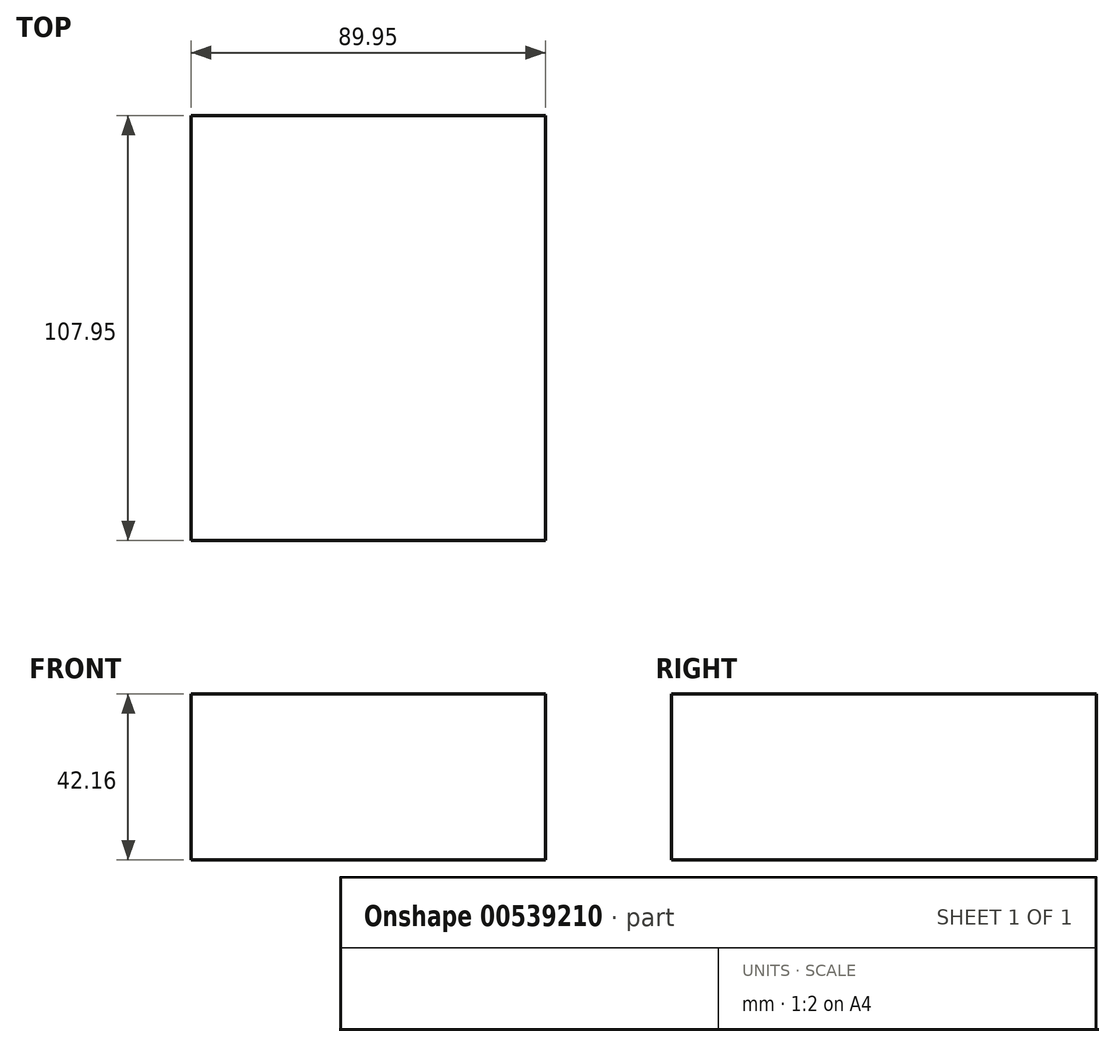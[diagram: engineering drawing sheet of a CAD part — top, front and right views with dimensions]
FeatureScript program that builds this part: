
annotation { "Feature Type Name" : "Feature", "Feature Type Description" : "" }
export const myFeature = defineFeature(function(context is Context, id is Id, definition is map)
    precondition{}
    {
        {
            var Q0;
            Q0=qCreatedBy(makeId("Top.planeOp"),FACE);
            var sketch = newSketch(context, id + "F0", { "sketchPlane" : qUnion([Q0])});
            skLineSegment(sketch, "E0.bottom", {"start": v(-52.77, 49.57) * mm, "end": v(37.18, 49.57) * mm});
            skLineSegment(sketch, "E0.top", {"start": v(-52.77, -58.38) * mm, "end": v(37.18, -58.38) * mm});
            skLineSegment(sketch, "E0.left", {"start": v(-52.77, 49.57) * mm, "end": v(-52.77, -58.38) * mm});
            skLineSegment(sketch, "E0.right", {"start": v(37.18, 49.57) * mm, "end": v(37.18, -58.38) * mm});
            skSolve(sketch);
        }
        {
            var Q0;
            Q0 = qSketchRegion(id + "F0", true);
            extrude(context, id + "F1", {"entities" : qUnion([Q0]), "depth" : 42.16 * mm, "offsetDistance" : 25.4 * mm});
        }
    });
